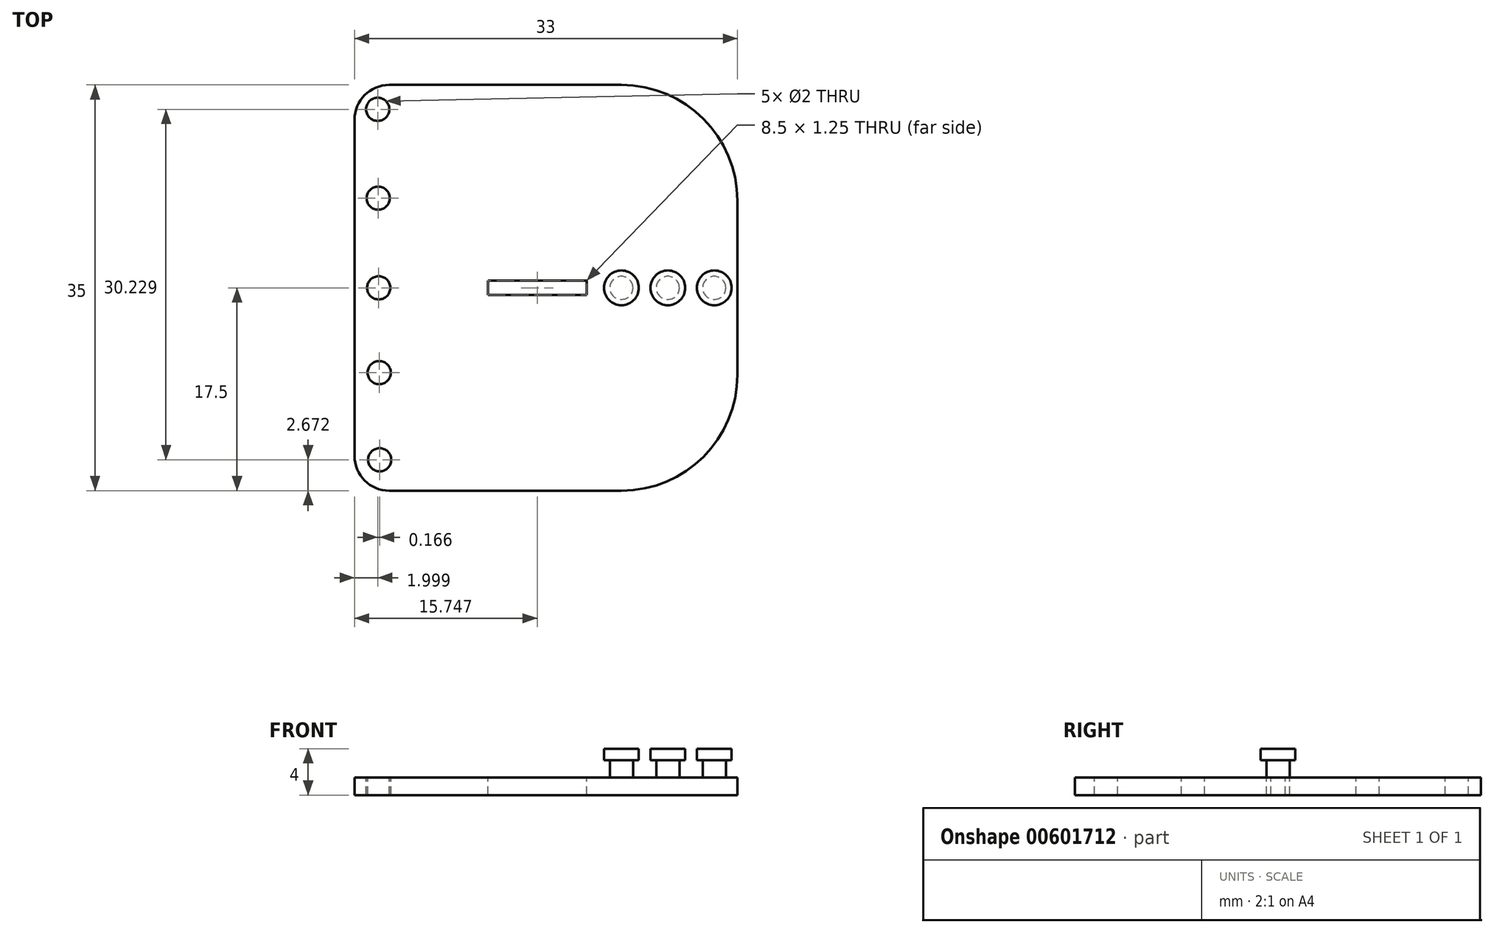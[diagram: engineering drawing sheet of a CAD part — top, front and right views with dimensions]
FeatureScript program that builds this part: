
annotation { "Feature Type Name" : "Feature", "Feature Type Description" : "" }
export const myFeature = defineFeature(function(context is Context, id is Id, definition is map)
    precondition{}
    {
        {
            var Q0;
            Q0=qCreatedBy(makeId("Top.planeOp"),FACE);
            var sketch = newSketch(context, id + "F0", { "sketchPlane" : qUnion([Q0])});
            skLineSegment(sketch, "E0.bottom", {"start": v(-11.1, 17.5) * mm, "end": v(21.9, 17.5) * mm});
            skLineSegment(sketch, "E0.top", {"start": v(-11.1, -17.5) * mm, "end": v(21.9, -17.5) * mm});
            skLineSegment(sketch, "E0.left", {"start": v(-11.1, 17.5) * mm, "end": v(-11.1, -17.5) * mm});
            skLineSegment(sketch, "E0.right", {"start": v(21.9, 17.5) * mm, "end": v(21.9, -17.5) * mm});
            skLineSegment(sketch, "E1.bottom", {"start": v(0.4, 0.63) * mm, "end": v(8.9, 0.63) * mm});
            skLineSegment(sketch, "E1.top", {"start": v(0.4, -0.62) * mm, "end": v(8.9, -0.62) * mm});
            skLineSegment(sketch, "E1.left", {"start": v(0.4, 0.63) * mm, "end": v(0.4, -0.62) * mm});
            skLineSegment(sketch, "E1.right", {"start": v(8.9, 0.63) * mm, "end": v(8.9, -0.62) * mm});
            skSolve(sketch);
        }
        {
            var Q0;
            Q0=makeQuery(id+"F0.imprint","IMPRINT",FACE,{"disambiguationData":[TD([[makeQuery(id+"F0.imprint","IMPRINT",EDGE,{"derivedFrom":sQuery(id+"F0.wireOp",EDGE,"E0.bottom")}),-1.0]])]});
            extrude(context, id + "F1", {"entities" : qUnion([Q0]), "oppositeDirection" : true, "depth" : 1.5 * mm, "offsetDistance" : 25 * mm});
        }
        {
            var Q0;
            Q0=makeQuery(id+"F1.opExtrude","CAP_FACE",FACE,{"disambiguationData":[OSD([sQuery(id+"F0.wireOp",EDGE,"E0.bottom"),sQuery(id+"F0.wireOp",EDGE,"E0.top"),sQuery(id+"F0.wireOp",EDGE,"E0.left"),sQuery(id+"F0.wireOp",EDGE,"E0.right"),sQuery(id+"F0.wireOp",EDGE,"E1.bottom"),sQuery(id+"F0.wireOp",EDGE,"E1.top"),sQuery(id+"F0.wireOp",EDGE,"E1.left"),sQuery(id+"F0.wireOp",EDGE,"E1.right")])],"isStart":true});
            var sketch = newSketch(context, id + "F2", { "sketchPlane" : qUnion([Q0])});
            skLineSegment(sketch, "E2", {"start": v(-9.13, 22.06) * mm, "end": v(-8.9, -21.04) * mm, "construction": true});
            skCircle(sketch, "E3", {"center": v(-9, 0) * mm, "radius": 1 * mm});
            skCircle(sketch, "E4", {"center": v(-9.1, 15.4) * mm, "radius": 1 * mm});
            skCircle(sketch, "E5", {"center": v(-9.05, 7.74) * mm, "radius": 1 * mm});
            skCircle(sketch, "E6", {"center": v(-8.92, -14.83) * mm, "radius": 1 * mm});
            skCircle(sketch, "E7", {"center": v(-8.97, -7.32) * mm, "radius": 1 * mm});
            skSolve(sketch);
        }
        {
            var Q0;
            Q0=makeQuery(id+"F2.imprint","IMPRINT",FACE,{"disambiguationData":[TD([[makeQuery(id+"F2.imprint","IMPRINT",EDGE,{"derivedFrom":sQuery(id+"F2.wireOp",EDGE,"E4")}),1.0]])]});
            var Q1;
            Q1=makeQuery(id+"F2.imprint","IMPRINT",FACE,{"disambiguationData":[TD([[makeQuery(id+"F2.imprint","IMPRINT",EDGE,{"derivedFrom":sQuery(id+"F2.wireOp",EDGE,"E5")}),1.0]])]});
            var Q2;
            Q2=makeQuery(id+"F2.imprint","IMPRINT",FACE,{"disambiguationData":[TD([[makeQuery(id+"F2.imprint","IMPRINT",EDGE,{"derivedFrom":sQuery(id+"F2.wireOp",EDGE,"E3")}),1.0]])]});
            var Q3;
            Q3=makeQuery(id+"F2.imprint","IMPRINT",FACE,{"disambiguationData":[TD([[makeQuery(id+"F2.imprint","IMPRINT",EDGE,{"derivedFrom":sQuery(id+"F2.wireOp",EDGE,"E7")}),1.0]])]});
            var Q4;
            Q4=makeQuery(id+"F2.imprint","IMPRINT",FACE,{"disambiguationData":[TD([[makeQuery(id+"F2.imprint","IMPRINT",EDGE,{"derivedFrom":sQuery(id+"F2.wireOp",EDGE,"E6")}),1.0]])]});
            extrude(context, id + "F3", {"entities" : qUnion([Q0, Q1, Q2, Q3, Q4]), "operationType" : NewBodyOperationType.REMOVE, "oppositeDirection" : true, "depth" : 1.5 * mm, "offsetDistance" : 25 * mm});
        }
        {
            var Q0;
            Q0=makeQuery(id+"F1.opExtrude","SWEPT_EDGE",EDGE,{"disambiguationData":[OSD([sQuery(id+"F0.wireOp",EDGE,"E0.top"),sQuery(id+"F0.wireOp",EDGE,"E0.left")])]});
            var Q1;
            Q1=makeQuery(id+"F1.opExtrude","SWEPT_EDGE",EDGE,{"disambiguationData":[OSD([sQuery(id+"F0.wireOp",EDGE,"E0.bottom"),sQuery(id+"F0.wireOp",EDGE,"E0.left")])]});
            fillet(context, id + "F4", {"entities" : qUnion([Q0, Q1]), "radius" : 3 * mm, "tangentPropagation" : true, "allowEdgeOverflow" : false});
        }
        {
            var Q0;
            Q0=makeQuery(id+"F1.opExtrude","SWEPT_EDGE",EDGE,{"disambiguationData":[OSD([sQuery(id+"F0.wireOp",EDGE,"E0.bottom"),sQuery(id+"F0.wireOp",EDGE,"E0.right")])]});
            var Q1;
            Q1=makeQuery(id+"F1.opExtrude","SWEPT_EDGE",EDGE,{"disambiguationData":[OSD([sQuery(id+"F0.wireOp",EDGE,"E0.top"),sQuery(id+"F0.wireOp",EDGE,"E0.right")])]});
            fillet(context, id + "F5", {"entities" : qUnion([Q0, Q1]), "radius" : 10 * mm, "tangentPropagation" : true, "allowEdgeOverflow" : false});
        }
        {
            var Q0;
            Q0=makeQuery(id+"F1.opExtrude","CAP_FACE",FACE,{"disambiguationData":[OSD([sQuery(id+"F0.wireOp",EDGE,"E0.bottom"),sQuery(id+"F0.wireOp",EDGE,"E0.top"),sQuery(id+"F0.wireOp",EDGE,"E0.left"),sQuery(id+"F0.wireOp",EDGE,"E0.right"),sQuery(id+"F0.wireOp",EDGE,"E1.bottom"),sQuery(id+"F0.wireOp",EDGE,"E1.top"),sQuery(id+"F0.wireOp",EDGE,"E1.left"),sQuery(id+"F0.wireOp",EDGE,"E1.right")])],"isStart":true});
            var sketch = newSketch(context, id + "F6", { "sketchPlane" : qUnion([Q0])});
            skCircle(sketch, "E8", {"center": v(19.9, 0) * mm, "radius": 1 * mm});
            skCircle(sketch, "E9", {"center": v(15.9, 0) * mm, "radius": 1 * mm});
            skCircle(sketch, "E10", {"center": v(11.9, 0) * mm, "radius": 1 * mm});
            skSolve(sketch);
        }
        {
            var Q0;
            Q0=makeQuery(id+"F6.imprint","IMPRINT",FACE,{"disambiguationData":[TD([[makeQuery(id+"F6.imprint","IMPRINT",EDGE,{"derivedFrom":sQuery(id+"F6.wireOp",EDGE,"E10")}),1.0]])]});
            var Q1;
            Q1=makeQuery(id+"F6.imprint","IMPRINT",FACE,{"disambiguationData":[TD([[makeQuery(id+"F6.imprint","IMPRINT",EDGE,{"derivedFrom":sQuery(id+"F6.wireOp",EDGE,"E9")}),1.0]])]});
            var Q2;
            Q2=makeQuery(id+"F6.imprint","IMPRINT",FACE,{"disambiguationData":[TD([[makeQuery(id+"F6.imprint","IMPRINT",EDGE,{"derivedFrom":sQuery(id+"F6.wireOp",EDGE,"E8")}),1.0]])]});
            extrude(context, id + "F7", {"entities" : qUnion([Q0, Q1, Q2]), "operationType" : NewBodyOperationType.ADD, "depth" : 1.5 * mm, "offsetDistance" : 25 * mm});
        }
        {
            var Q0;
            Q0=makeQuery(id+"F7.opExtrude","CAP_FACE",FACE,{"disambiguationData":[OSD([sQuery(id+"F6.wireOp",EDGE,"E10")])],"isStart":false});
            var sketch = newSketch(context, id + "F8", { "sketchPlane" : qUnion([Q0])});
            skCircle(sketch, "E11", {"center": v(11.9, 0) * mm, "radius": 1.5 * mm});
            skSolve(sketch);
        }
        {
            var Q0;
            Q0=makeQuery(id+"F8.imprint","IMPRINT",FACE,{"disambiguationData":[TD([[makeQuery(id+"F8.imprint","IMPRINT",EDGE,{"derivedFrom":makeQuery(id+"F7.opExtrude","CAP_EDGE",EDGE,{"disambiguationData":[OSD([sQuery(id+"F6.wireOp",EDGE,"E10")])],"isStart":false})}),1.0]])]});
            var Q1;
            Q1=makeQuery(id+"F8.imprint","IMPRINT",FACE,{"disambiguationData":[TD([[makeQuery(id+"F8.imprint","IMPRINT",EDGE,{"derivedFrom":sQuery(id+"F8.wireOp",EDGE,"E11")}),1.0]])]});
            extrude(context, id + "F9", {"entities" : qUnion([Q0, Q1]), "depth" : 1 * mm, "offsetDistance" : 25 * mm});
        }
        {
            var Q0;
            Q0=makeQuery(id+"F7.opExtrude","CAP_FACE",FACE,{"disambiguationData":[OSD([sQuery(id+"F6.wireOp",EDGE,"E9")])],"isStart":false});
            var sketch = newSketch(context, id + "F10", { "sketchPlane" : qUnion([Q0])});
            skCircle(sketch, "E12", {"center": v(15.9, 0) * mm, "radius": 1.5 * mm});
            skSolve(sketch);
        }
        {
            var Q0;
            Q0=makeQuery(id+"F10.imprint","IMPRINT",FACE,{"disambiguationData":[TD([[makeQuery(id+"F10.imprint","IMPRINT",EDGE,{"derivedFrom":sQuery(id+"F10.wireOp",EDGE,"E12")}),1.0]])]});
            var Q1;
            Q1=makeQuery(id+"F10.imprint","IMPRINT",FACE,{"disambiguationData":[TD([[makeQuery(id+"F10.imprint","IMPRINT",EDGE,{"derivedFrom":makeQuery(id+"F7.opExtrude","CAP_EDGE",EDGE,{"disambiguationData":[OSD([sQuery(id+"F6.wireOp",EDGE,"E9")])],"isStart":false})}),1.0]])]});
            extrude(context, id + "F11", {"entities" : qUnion([Q0, Q1]), "operationType" : NewBodyOperationType.ADD, "depth" : 1 * mm, "offsetDistance" : 25 * mm});
        }
        {
            var Q0;
            Q0=makeQuery(id+"F7.opExtrude","CAP_FACE",FACE,{"disambiguationData":[OSD([sQuery(id+"F6.wireOp",EDGE,"E8")])],"isStart":false});
            var sketch = newSketch(context, id + "F12", { "sketchPlane" : qUnion([Q0])});
            skCircle(sketch, "E13", {"center": v(19.9, 0) * mm, "radius": 1.5 * mm});
            skSolve(sketch);
        }
        {
            var Q0;
            Q0=makeQuery(id+"F12.imprint","IMPRINT",FACE,{"disambiguationData":[TD([[makeQuery(id+"F12.imprint","IMPRINT",EDGE,{"derivedFrom":makeQuery(id+"F7.opExtrude","CAP_EDGE",EDGE,{"disambiguationData":[OSD([sQuery(id+"F6.wireOp",EDGE,"E8")])],"isStart":false})}),1.0]])]});
            var Q1;
            Q1=makeQuery(id+"F12.imprint","IMPRINT",FACE,{"disambiguationData":[TD([[makeQuery(id+"F12.imprint","IMPRINT",EDGE,{"derivedFrom":sQuery(id+"F12.wireOp",EDGE,"E13")}),1.0]])]});
            extrude(context, id + "F13", {"entities" : qUnion([Q0, Q1]), "operationType" : NewBodyOperationType.ADD, "depth" : 1 * mm, "offsetDistance" : 25 * mm});
        }
    });
